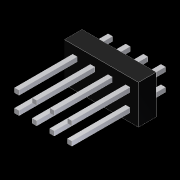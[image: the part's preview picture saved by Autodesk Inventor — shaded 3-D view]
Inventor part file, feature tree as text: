
AUTODESK INVENTOR PART (.ipt)
format: ipt  version: 2012 (Build 160160000, 160)  size: 127,488 bytes
history: native  units: in
note: dims shown in document units (in); Inventor stores cm internally (conversion verified against a paired STEP export)
features: extrude x3, sketch x1, pattern_linear x1
ambient origin geometry x8: Origin, YZ Plane, XZ Plane, XY Plane, X Axis, Y Axis, Z Axis, Center Point
bodies: Solid1 (feature_tree)
feature tree (5):
  sketch  "Sketch1"  dims[d0=0.1in d1=0.0in d2=0.33in d3=0.0in d4=0.2in d5=0.0in d6=1.5748in d8=0.1in d9=0.7874in d11=0.1in]
  extrude  "Extrusion1"  Depth=0.33in TaperAngle=0.0deg
  extrude  "Extrusion2"  Depth=0.2in TaperAngle=0.0deg
  extrude  "Extrusion3"  Depth=1.5748in
  pattern_linear  "Rectangular Pattern1"  Count1=2 Spacing1=0.1in
